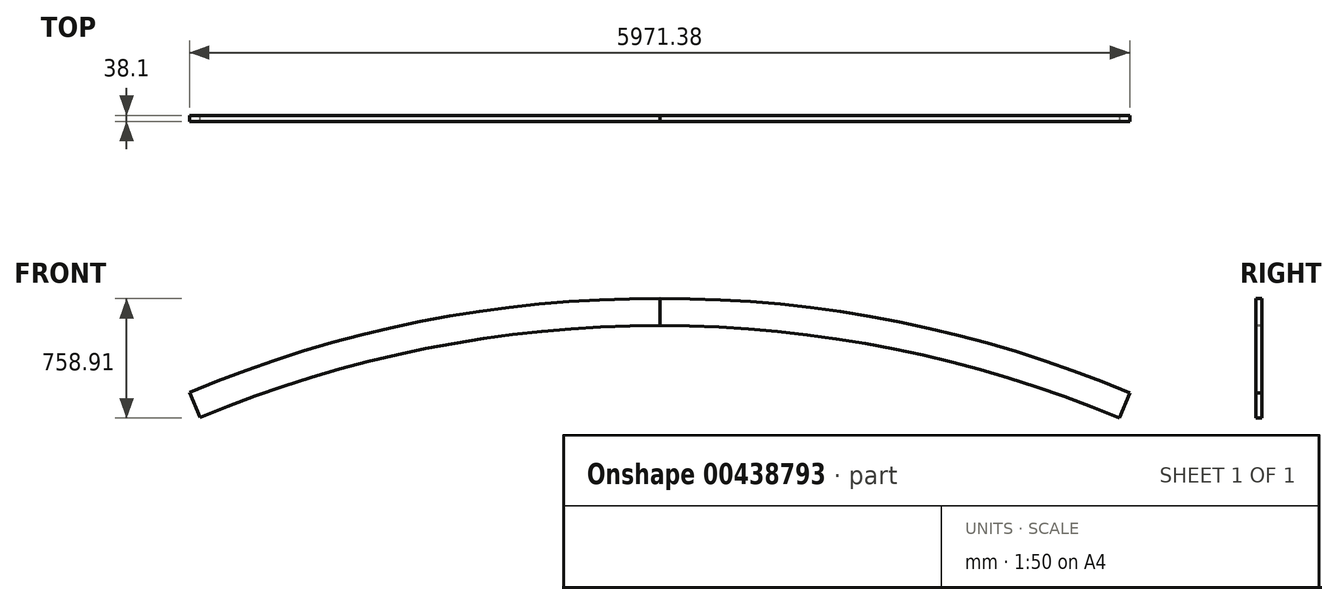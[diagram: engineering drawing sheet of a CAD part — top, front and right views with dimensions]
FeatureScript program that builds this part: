
annotation { "Feature Type Name" : "Feature", "Feature Type Description" : "" }
export const myFeature = defineFeature(function(context is Context, id is Id, definition is map)
    precondition{}
    {
        {
            var Q0;
            Q0=qCreatedBy(makeId("Front.planeOp"),FACE);
            var sketch = newSketch(context, id + "F0", { "sketchPlane" : qUnion([Q0])});
            skArc(sketch, "E0", {"start": v(1516.23, 9.78) * mm, "mid": v(27.46, 157.77) * mm, "end": v(-1461.37, 10.36) * mm});
            skArc(sketch, "E1", {"start": v(1549.98, 178.04) * mm, "mid": v(25.98, 332.88) * mm, "end": v(-1498.02, 178.04) * mm});
            skPoint(sketch, "E2.MirrorCS.start.orphan", {"position": v(20.45, 2.93) * mm});
            skPoint(sketch, "E3.end.orphan", {"position": v(25.98, 332.88) * mm});
            skPoint(sketch, "E4.top.start.orphan", {"position": v(25.98, 178.04) * mm});
            skLineSegment(sketch, "E5", {"start": v(-1498.02, 193.43) * mm, "end": v(-1461.37, 10.36) * mm});
            skLineSegment(sketch, "E6", {"start": v(1549.98, 178.04) * mm, "end": v(1516.23, 9.78) * mm});
            skLineSegment(sketch, "E7", {"start": v(-1238.89, 51.45) * mm, "end": v(1232.72, 61.06) * mm});
            skSolve(sketch);
        }
        {
            var Q0;
            Q0=makeQuery(id+"F0.imprint","IMPRINT",FACE,{"disambiguationData":[TD([[makeQuery(id+"F0.imprint","IMPRINT",EDGE,{"derivedFrom":sQuery(id+"F0.wireOp",EDGE,"E0")}),-1.0]])]});
            extrude(context, id + "F1", {"entities" : qUnion([Q0]), "depth" : 38.1 * mm});
        }
        {
            var Q0;
            Q0=makeQuery(id+"F1.opExtrude","SWEPT_BODY",BODY,{"disambiguationData":[OSD([sQuery(id+"F0.wireOp",EDGE,"E0"),sQuery(id+"F0.wireOp",EDGE,"E1"),sQuery(id+"F0.wireOp",EDGE,"E5"),sQuery(id+"F0.wireOp",EDGE,"E6")])]});
            var Q1;
            Q1=makeQuery(id+"F1.opExtrude","CAP_EDGE",EDGE,{"disambiguationData":[OSD([sQuery(id+"F0.wireOp",EDGE,"E1")])],"isStart":false});
            var Q2;
            Q2=makeQuery(id+"F1.opExtrude","CAP_EDGE",EDGE,{"disambiguationData":[OSD([sQuery(id+"F0.wireOp",EDGE,"E6")])],"isStart":false});
            transform(context, id + "F2", {"entities" : qUnion([Q0]), "transformType" : TransformType.ROTATION, "transformAxis" : qUnion([Q2]), "angle" : 180 * degree, "makeCopy" : true});
        }
        {
            var Q0;
            Q0=makeQuery(id+"F2.opPattern","COPY",BODY,{"derivedFrom":makeQuery(id+"F1.opExtrude","SWEPT_BODY",BODY,{"disambiguationData":[OSD([sQuery(id+"F0.wireOp",EDGE,"E0"),sQuery(id+"F0.wireOp",EDGE,"E1"),sQuery(id+"F0.wireOp",EDGE,"E5"),sQuery(id+"F0.wireOp",EDGE,"E6")])]}),"instanceName":"1"});
            transform(context, id + "F3", {"entities" : qUnion([Q0]), "transformType" : TransformType.TRANSLATION_3D, "dx" : 0 * mm, "dy" : 38.1 * mm, "dz" : 0 * mm, "makeCopy" : false});
        }
        {
            var Q0;
            Q0=makeQuery(id+"F1.opExtrude","SWEPT_BODY",BODY,{"disambiguationData":[OSD([sQuery(id+"F0.wireOp",EDGE,"E0"),sQuery(id+"F0.wireOp",EDGE,"E1"),sQuery(id+"F0.wireOp",EDGE,"E5"),sQuery(id+"F0.wireOp",EDGE,"E6")])]});
            var Q1;
            Q1=makeQuery(id+"F2.opPattern","COPY",BODY,{"derivedFrom":makeQuery(id+"F1.opExtrude","SWEPT_BODY",BODY,{"disambiguationData":[OSD([sQuery(id+"F0.wireOp",EDGE,"E0"),sQuery(id+"F0.wireOp",EDGE,"E1"),sQuery(id+"F0.wireOp",EDGE,"E5"),sQuery(id+"F0.wireOp",EDGE,"E6")])]}),"instanceName":"1"});
            var Q2;
            Q2=makeQuery(id+"F1.opExtrude","SWEPT_EDGE",EDGE,{"disambiguationData":[OSD([sQuery(id+"F0.wireOp",EDGE,"E1"),sQuery(id+"F0.wireOp",EDGE,"E5")])]});
            transform(context, id + "F4", {"entities" : qUnion([Q0, Q1]), "transformType" : TransformType.ROTATION, "transformAxis" : qUnion([Q2]), "angle" : 11.3 * degree, "oppositeDirection" : true, "makeCopy" : false});
        }
    });
